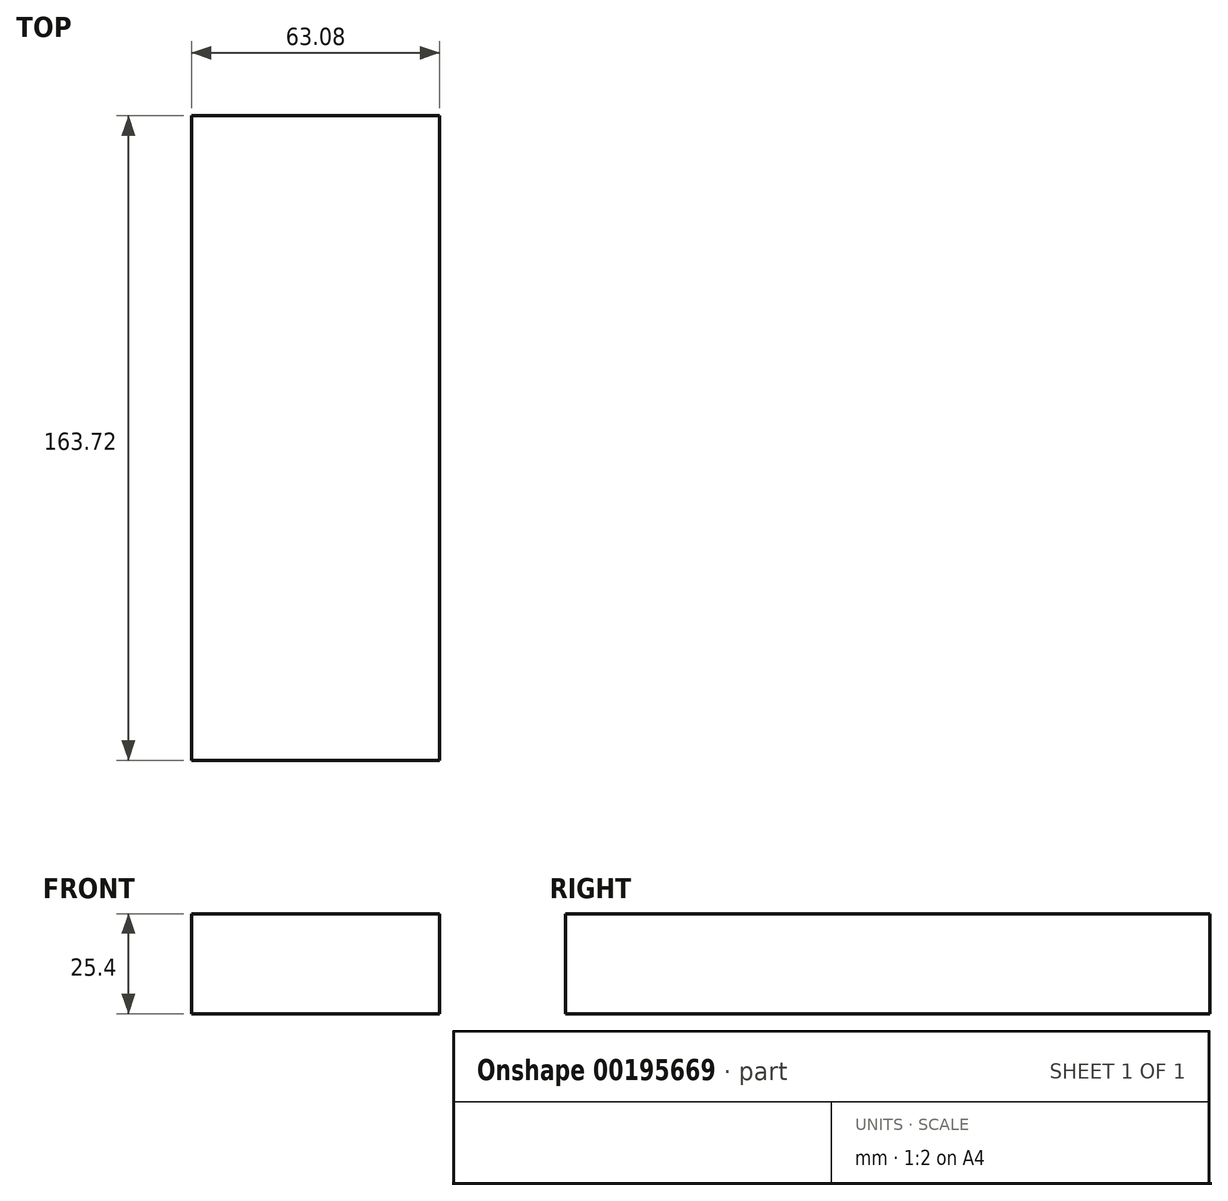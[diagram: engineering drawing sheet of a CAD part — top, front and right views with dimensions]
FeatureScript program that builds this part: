
annotation { "Feature Type Name" : "Feature", "Feature Type Description" : "" }
export const myFeature = defineFeature(function(context is Context, id is Id, definition is map)
    precondition{}
    {
        {
            var Q0;
            Q0=qCreatedBy(makeId("Top.planeOp"),FACE);
            var sketch = newSketch(context, id + "F0", { "sketchPlane" : qUnion([Q0])});
            skLineSegment(sketch, "E0.bottom", {"start": v(0, 0) * mm, "end": v(-63.08, 0) * mm});
            skLineSegment(sketch, "E0.top", {"start": v(0, 163.72) * mm, "end": v(-63.08, 163.72) * mm});
            skLineSegment(sketch, "E0.left", {"start": v(0, 0) * mm, "end": v(0, 163.72) * mm});
            skLineSegment(sketch, "E0.right", {"start": v(-63.08, 0) * mm, "end": v(-63.08, 163.72) * mm});
            skPoint(sketch, "E0.middle", {"position": v(-31.54, 81.86) * mm});
            skSolve(sketch);
        }
        {
            var Q0;
            Q0=makeQuery(id+"F0.imprint","IMPRINT",FACE,{"disambiguationData":[TD([[makeQuery(id+"F0.imprint","IMPRINT",EDGE,{"derivedFrom":sQuery(id+"F0.wireOp",EDGE,"E0.bottom")}),-1.0]])]});
            extrude(context, id + "F1", {"entities" : qUnion([Q0]), "depth" : 25.4 * mm});
        }
    });
